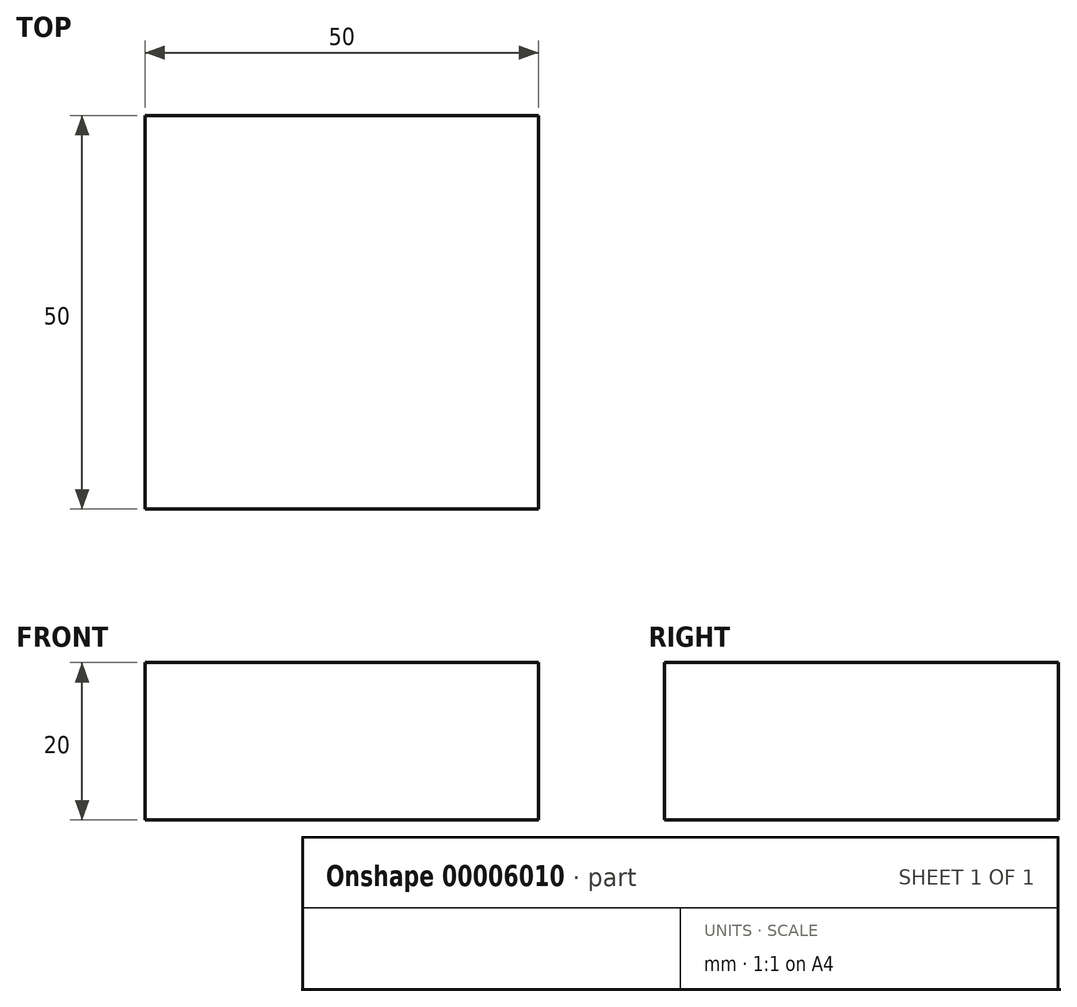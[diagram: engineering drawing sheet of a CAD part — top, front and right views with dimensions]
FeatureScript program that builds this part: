
annotation { "Feature Type Name" : "Feature", "Feature Type Description" : "" }
export const myFeature = defineFeature(function(context is Context, id is Id, definition is map)
    precondition{}
    {
        {
            var Q0;
            Q0=qCreatedBy(makeId("Top.planeOp"),FACE);
            var sketch = newSketch(context, id + "F0", { "sketchPlane" : qUnion([Q0])});
            skLineSegment(sketch, "E0.bottom", {"start": v(0, 0) * mm, "end": v(50, 0) * mm});
            skLineSegment(sketch, "E0.top", {"start": v(0, 50) * mm, "end": v(50, 50) * mm});
            skLineSegment(sketch, "E0.left", {"start": v(0, 0) * mm, "end": v(0, 50) * mm});
            skLineSegment(sketch, "E0.right", {"start": v(50, 0) * mm, "end": v(50, 50) * mm});
            skSolve(sketch);
        }
        {
            var Q0;
            Q0=makeQuery(id+"F0.imprint","IMPRINT",FACE,{"disambiguationData":[TD([[makeQuery(id+"F0.imprint","IMPRINT",EDGE,{"derivedFrom":sQuery(id+"F0.wireOp",EDGE,"E0.bottom")}),1.0]])]});
            extrude(context, id + "F1", {"entities" : qUnion([Q0]), "depth" : 20 * mm});
        }
    });
